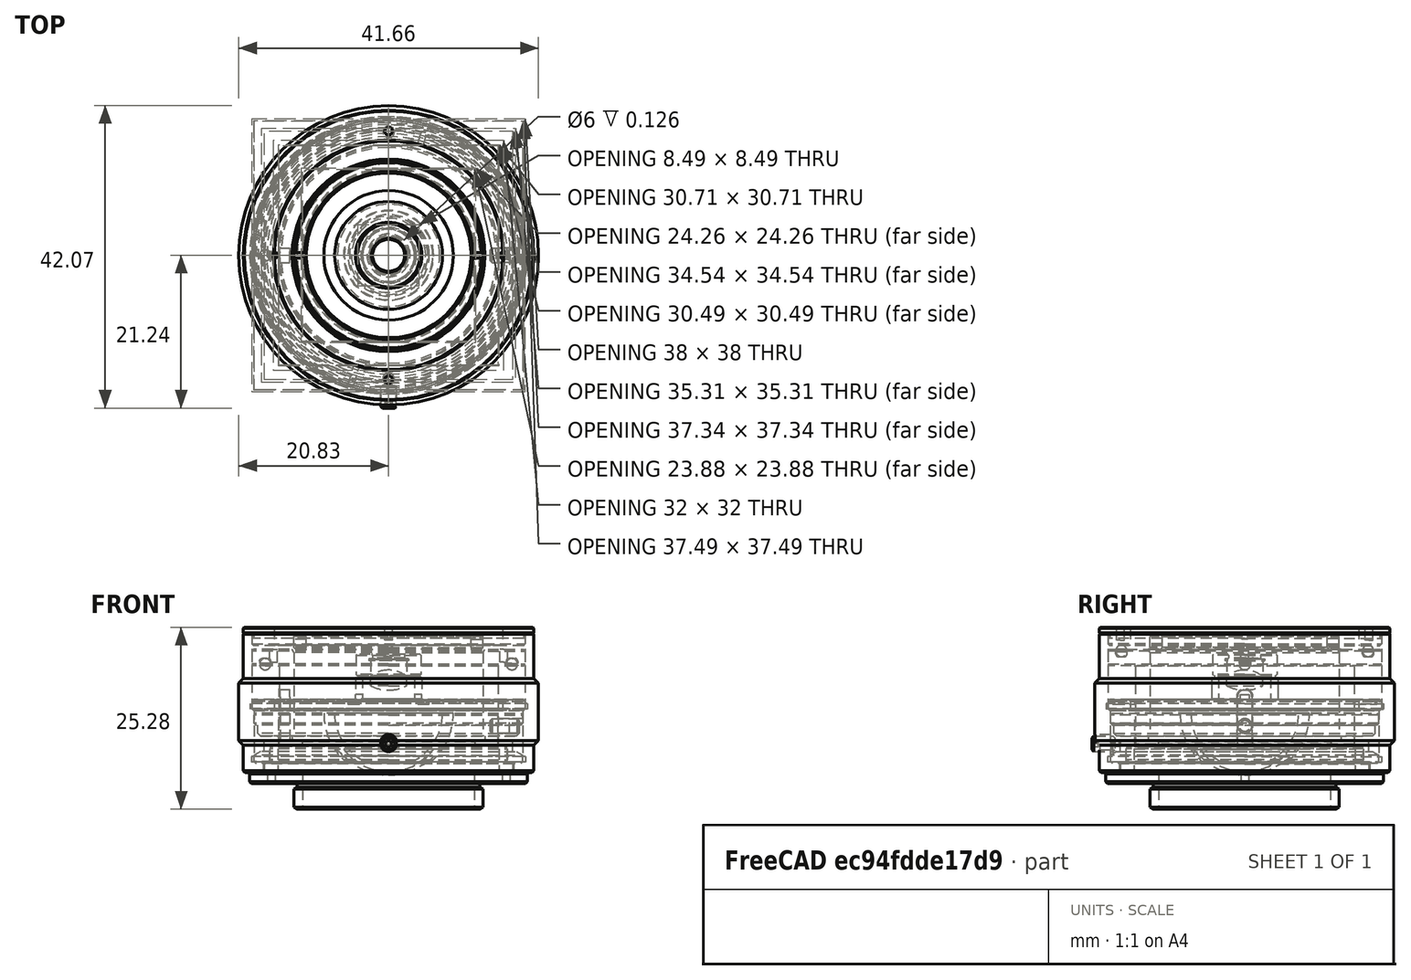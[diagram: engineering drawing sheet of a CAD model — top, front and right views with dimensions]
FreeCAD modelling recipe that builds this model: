
FCSTD DOCUMENT  (FreeCAD 0.18.4R)
Label: mush
License: All rights reserved
LicenseURL: http://en.wikipedia.org/wiki/All_rights_reserved
objects: Part::Feature×14, Part::Cut×9, Part::Sphere×6, App::DocumentObjectGroup×4, Part::Box×4, Mesh::Feature×3, PartDesign::Body×2, Part::MultiFuse×1
note: 36 computed .brp shape members not serialized (recipe doc carries the construction recipe); baked Part::Feature solids carry a one-line shape summary decoded from their .brp

FEATURE [Part::Feature] Part__Feature  label="bague exterieure"
  Placement = pos=(0,0,0.2) rot=(0,0,1;0rad)
  shape: bbox 41.66 x 41.66 x 19.51 mm, 37 faces (baked)
FEATURE [Part::Feature] Part__Feature001  label="0538-E0W001"
  shape: bbox 37.33 x 37.33 x 6.985 mm, 36 faces (baked)
FEATURE [Part::Feature] Part__Feature002  label="baguefixation"
  shape: bbox 38.61 x 38.61 x 8.382 mm, 38 faces (baked)
FEATURE [Part::Feature] Part__Feature003  label="0538-E0W003"
  shape: bbox 38 x 38 x 13.46 mm, 63 faces (baked)
FEATURE [Part::Feature] Part__Feature004  label="fixation nob"
  shape: bbox 4 x 2 x 2 mm, 8 faces (baked)
FEATURE [Part::Feature] Part__Feature005  label="bague top"
  shape: bbox 40.39 x 40.39 x 2.54 mm, 28 faces (baked)
FEATURE [Part::Feature] Part__Feature006  label="blocking nob"
  shape: bbox 2.184 x 3.969 x 2.184 mm, 20 faces (baked)
FEATURE [Part::Feature] Part__Feature007  label="anneau de serrage"
  Placement = pos=(0,0,2) rot=(0,0,1;0rad)
  shape: bbox 26.29 x 26.29 x 2.032 mm, 23 faces (baked)
FEATURE [Part::Feature] Part__Feature008  label="amortisseur3"
  shape: bbox 1.588 x 1.588 x 1.588 mm, 2 faces (baked)
FEATURE [Part::Feature] Part__Feature009  label="amortisseur2"
  shape: bbox 1.588 x 1.588 x 1.588 mm, 2 faces (baked)
FEATURE [Part::Feature] Part__Feature010  label="amortisseur1"
  shape: bbox 1.588 x 1.588 x 1.588 mm, 2 faces (baked)
FEATURE [Part::Feature] Part__Feature011  label="amortisseur0"
  shape: bbox 1.588 x 1.588 x 1.588 mm, 2 faces (baked)
FEATURE [Part::Feature] Part__Feature012  label="0538-E0W012"
  shape: bbox 38 x 38 x 1.524 mm, 21 faces (baked)
FEATURE [App::DocumentObjectGroup] Groupe002  label="fixed part"
  Group = -> [Part__Feature,Part__Feature001,Part__Feature002,Part__Feature004,Part__Feature005,Part__Feature006,Part__Feature012]
FEATURE [Part::Sphere] Sphere  label="Sphère"
  Angle1 = -90
  Angle2 = 90
  Angle3 = 360
  AttacherType = Attacher::AttachEngine3D
  Radius = 8.6
FEATURE [Part::MultiFuse] Fusion
  Placement = pos=(0,0,2) rot=(0,0,1;0rad)
  Shapes = -> [Part__Feature011,Part__Feature010,Part__Feature009,Part__Feature008,Part__Feature007,Part__Feature003]
FEATURE [App::DocumentObjectGroup] Groupe001  label="mobile part"
  Group = -> [Fusion]
FEATURE [App::DocumentObjectGroup] Groupe  label="Zoom"
  Group = -> [Groupe001,Groupe002]
FEATURE [Part::Box] Box  label="Cube"
  AttacherType = Attacher::AttachEngine3D
  Height = 19
  Length = 20
  Placement = pos=(-10,-10,-6) rot=(0,0,1;0rad)
  Width = 20
FEATURE [Part::Sphere] Sphere001  label="Sphère001"
  Angle1 = -90
  Angle2 = 90
  Angle3 = 360
  AttacherType = Attacher::AttachEngine3D
  Radius = 8.1
FEATURE [Part::Cut] Cut
  Base = -> Sphere
  Tool = -> Sphere001
FEATURE [Part::Cut] Cut001  label="contact lens"
  Base = -> Cut
  Tool = -> Box
FEATURE [Part::Sphere] Sphere002  label="Sphère002"
  Angle1 = -90
  Angle2 = 90
  Angle3 = 360
  AttacherType = Attacher::AttachEngine3D
  Radius = 8.7
FEATURE [Part::Box] Box001  label="Cube001"
  AttacherType = Attacher::AttachEngine3D
  Height = 19
  Length = 20
  Placement = pos=(-10,-10,-5) rot=(0,0,1;0rad)
  Width = 20
FEATURE [Part::Sphere] Sphere003  label="Sphère003"
  Angle1 = -90
  Angle2 = 90
  Angle3 = 360
  AttacherType = Attacher::AttachEngine3D
  Radius = 8
FEATURE [Part::Cut] Cut002
  Base = -> Sphere002
  Tool = -> Sphere003
FEATURE [Part::Cut] Cut003  label="contact lens001"
  Base = -> Cut002
  Tool = -> Box001
FEATURE [Part::Sphere] Sphere004  label="Sphère004"
  Angle1 = -90
  Angle2 = 90
  Angle3 = 360
  AttacherType = Attacher::AttachEngine3D
  Radius = 9
FEATURE [Part::Sphere] Sphere005  label="Sphère005"
  Angle1 = -90
  Angle2 = 90
  Angle3 = 360
  AttacherType = Attacher::AttachEngine3D
  Radius = 7.5
FEATURE [Part::Cut] Cut004
  Base = -> Sphere004
  Tool = -> Sphere005
FEATURE [Part::Box] Box002  label="Cube002"
  AttacherType = Attacher::AttachEngine3D
  Height = 20
  Length = 20
  Placement = pos=(-10,-10,0) rot=(0,0,1;0rad)
  Width = 20
FEATURE [Part::Cut] Cut005
  Base = -> Cut004
  Tool = -> Box002
FEATURE [Part::Cut] Cut006
  Base = -> Cut005
FEATURE [Part::Cut] Cut007
  Base = -> Cut006
  Tool = -> Cut003
FEATURE [Part::Box] Box003  label="Cube003"
  AttacherType = Attacher::AttachEngine3D
  Height = 4
  Length = 15
  Placement = pos=(-7.5,-7.5,-11) rot=(0,0,1;0rad)
  Width = 15
FEATURE [Part::Cut] Cut008
  Base = -> Cut007
  Tool = -> Box003
FEATURE [Mesh::Feature] camera
  Placement = pos=(0,0,-4) rot=(0,0,1;0rad)
FEATURE [Mesh::Feature] cam_support
  Placement = pos=(0,0,-6) rot=(0,0,1;0rad)
FEATURE [Part::Feature] Part__Feature013  label="22558-E0W"
  Placement = pos=(0,0,5) rot=(0,1,0;3.14159rad)
  shape: bbox 9.238 x 9.238 x 6.35 mm, 91 faces, 3 solids (baked)
FEATURE [App::DocumentObjectGroup] Groupe003  label="camera_module"
  Group = -> [camera,cam_support]
FEATURE [Mesh::Feature] turret
  Placement = pos=(0,0,16.1) rot=(0,0,1;0rad)
FEATURE [PartDesign::Body] Body
  Origin = -> Origin
FEATURE [PartDesign::Body] Body001
  Origin = -> Origin001
